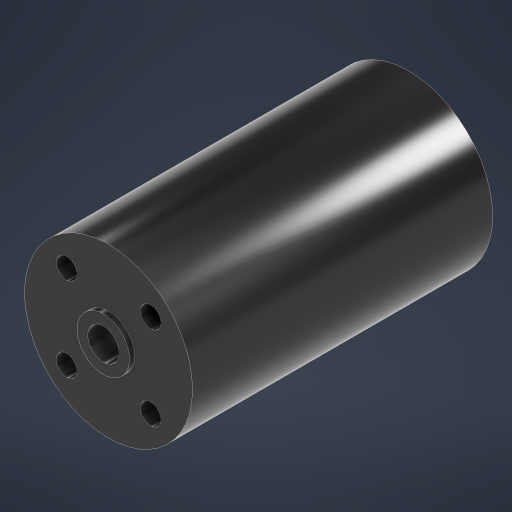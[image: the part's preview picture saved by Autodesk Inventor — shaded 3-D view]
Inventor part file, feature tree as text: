
AUTODESK INVENTOR PART (.ipt)
format: ipt  version: 2023.2 (Build 272271000, 271)  size: 257,536 bytes
history: native  units: mm
features: extrude x4, sketch x1, mirror x1
ambient origin geometry x8: Origin, YZ Plane, XZ Plane, XY Plane, X Axis, Y Axis, Z Axis, Center Point
bodies: Volumenkörper1 (feature_tree)
feature tree (6):
  sketch  "Skizze1"  dims[d0=32.0mm d1=4.0mm d2=8.0mm d3=8.0mm d4=20.0mm d6=16.0mm d7=20.0mm d9=16.0mm d12=57.2mm d13=0.0mm d14=10.0mm d15=0.0mm d16=10.0mm d17=1.0mm d18=0.0mm d19=6.0mm d20=0.0mm d21=0.0mm]
  extrude  "Extrusion1"  Depth=1.0mm
  extrude  "Extrusion2"  Depth=1.0mm
  extrude  "Extrusion3"  Depth=1.0mm
  extrude  "Extrusion4"  Depth=16.0mm
  mirror  "Spiegeln1"
